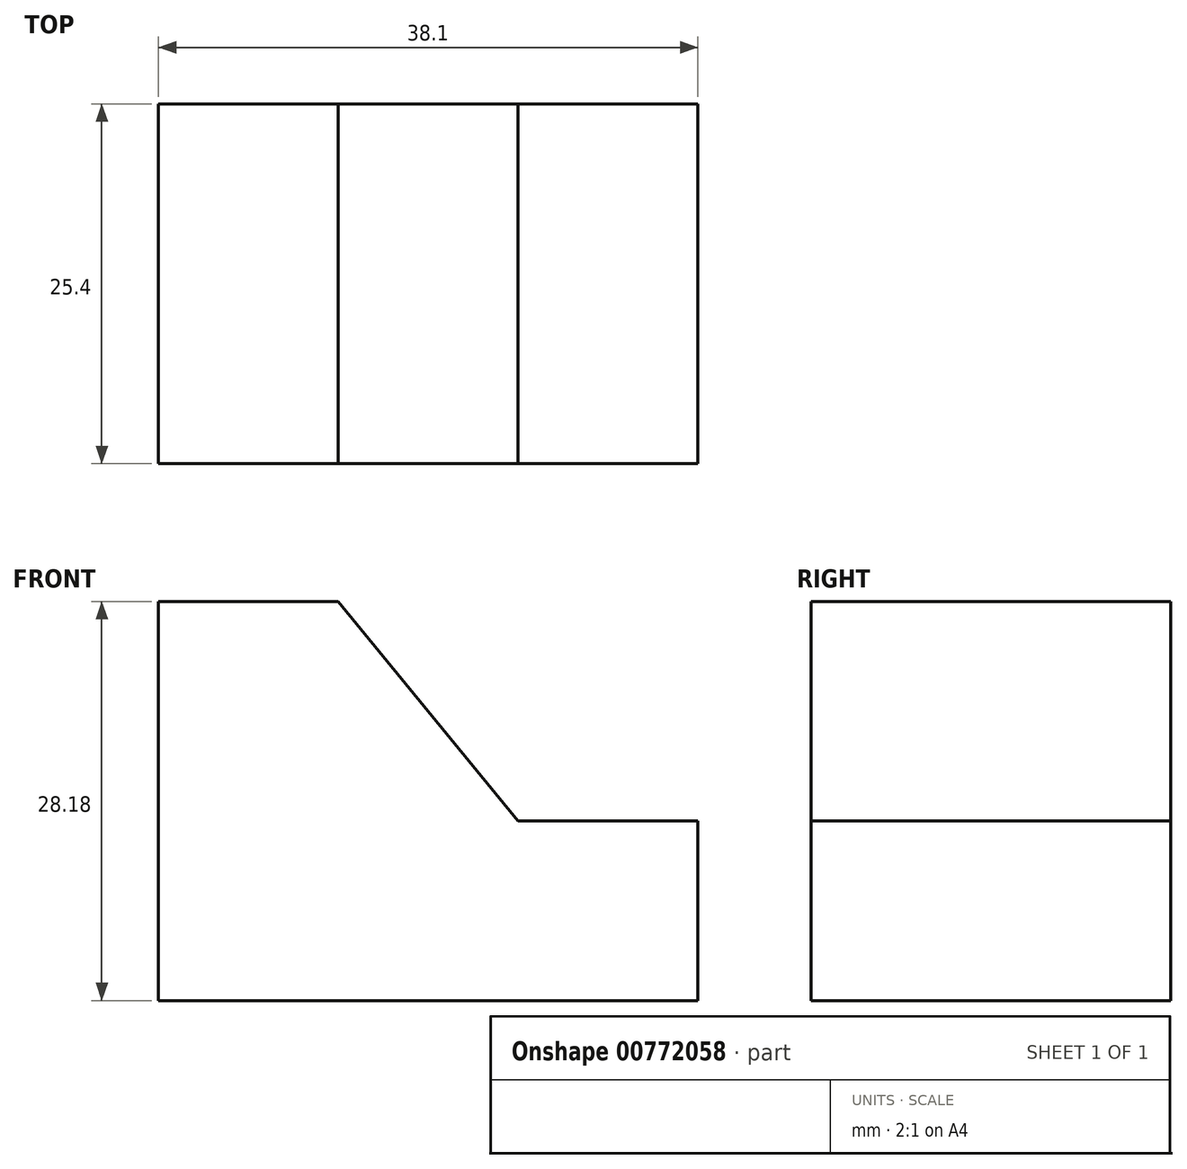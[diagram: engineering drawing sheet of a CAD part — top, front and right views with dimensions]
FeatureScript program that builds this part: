
annotation { "Feature Type Name" : "Feature", "Feature Type Description" : "" }
export const myFeature = defineFeature(function(context is Context, id is Id, definition is map)
    precondition{}
    {
        {
            var Q0;
            Q0=qCreatedBy(makeId("Front.planeOp"),FACE);
            var sketch = newSketch(context, id + "F0", { "sketchPlane" : qUnion([Q0])});
            skLineSegment(sketch, "E0", {"start": v(0, 0) * mm, "end": v(38.1, 0) * mm});
            skLineSegment(sketch, "E1", {"start": v(38.1, 0) * mm, "end": v(38.1, 12.7) * mm});
            skPoint(sketch, "E1.endSnap0", {"position": v(0, 12.7) * mm});
            skLineSegment(sketch, "E2", {"start": v(0, -3.57) * mm, "end": v(0, 28.18) * mm});
            skLineSegment(sketch, "E3", {"start": v(0, 28.18) * mm, "end": v(12.7, 28.18) * mm});
            skLineSegment(sketch, "E4", {"start": v(12.7, 28.18) * mm, "end": v(25.4, 12.7) * mm});
            skLineSegment(sketch, "E5", {"start": v(25.4, 12.7) * mm, "end": v(38.1, 12.7) * mm});
            skSolve(sketch);
        }
        {
            var Q0;
            {var subQ2=sQuery(id+"F0.wireOp",EDGE,"E0");Q0=makeQuery(id+"F0.imprint","IMPRINT",FACE,{"disambiguationData":[TD([[makeQuery(id+"F0.imprint","IMPRINT",EDGE,{"derivedFrom":subQ2}),1.0]])]});}
            extrude(context, id + "F1", {"entities" : qUnion([Q0]), "depth" : 25.4 * mm, "offsetDistance" : 25.4 * mm});
        }
    });
